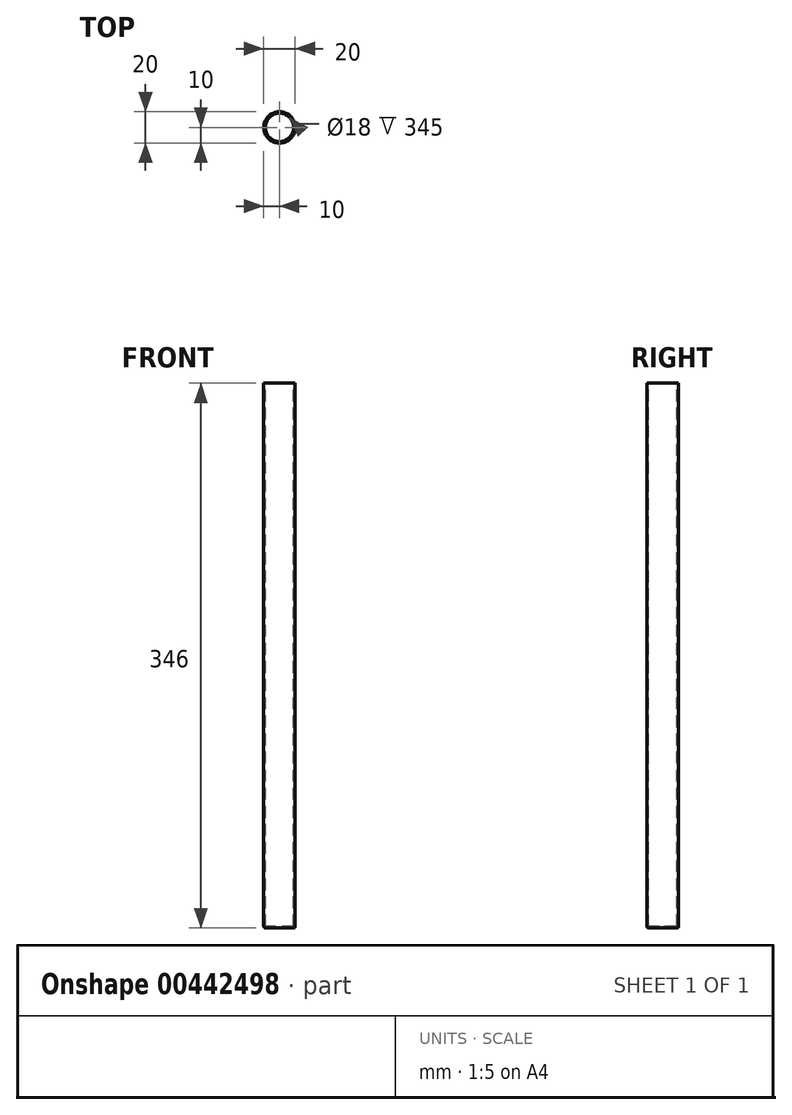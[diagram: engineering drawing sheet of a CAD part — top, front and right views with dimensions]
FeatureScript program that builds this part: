
annotation { "Feature Type Name" : "Feature", "Feature Type Description" : "" }
export const myFeature = defineFeature(function(context is Context, id is Id, definition is map)
    precondition{}
    {
        {
            var Q0;
            Q0=qCreatedBy(makeId("Top.planeOp"),FACE);
            var sketch = newSketch(context, id + "F0", { "sketchPlane" : qUnion([Q0])});
            skCircle(sketch, "E0", {"center": v(0, 0) * mm, "radius": 9 * mm});
            skSolve(sketch);
        }
        {
            var Q0;
            Q0=makeQuery(id+"F0.imprint","IMPRINT",FACE,{"disambiguationData":[TD([[makeQuery(id+"F0.imprint","IMPRINT",EDGE,{"derivedFrom":sQuery(id+"F0.wireOp",EDGE,"E0")}),1.0]])]});
            extrude(context, id + "F1", {"entities" : qUnion([Q0]), "oppositeDirection" : true, "depth" : 345 * mm});
        }
        {
            var Q0;
            Q0=makeQuery(id+"F1.opExtrude","CAP_FACE",FACE,{"disambiguationData":[OSD([sQuery(id+"F0.wireOp",EDGE,"E0")])],"isStart":true});
            shell(context, id + "F2", {"entities" : qUnion([Q0]), "thickness" : 1 * mm, "oppositeDirection" : true});
        }
        {
            var Q0;
            Q0=makeQuery(id+"F1.opExtrude","CAP_EDGE",EDGE,{"disambiguationData":[OSD([sQuery(id+"F0.wireOp",EDGE,"E0")])],"isStart":false});
            fillet(context, id + "F3", {"entities" : qUnion([Q0]), "radius" : 1 * mm, "tangentPropagation" : true, "allowEdgeOverflow" : false});
        }
    });
